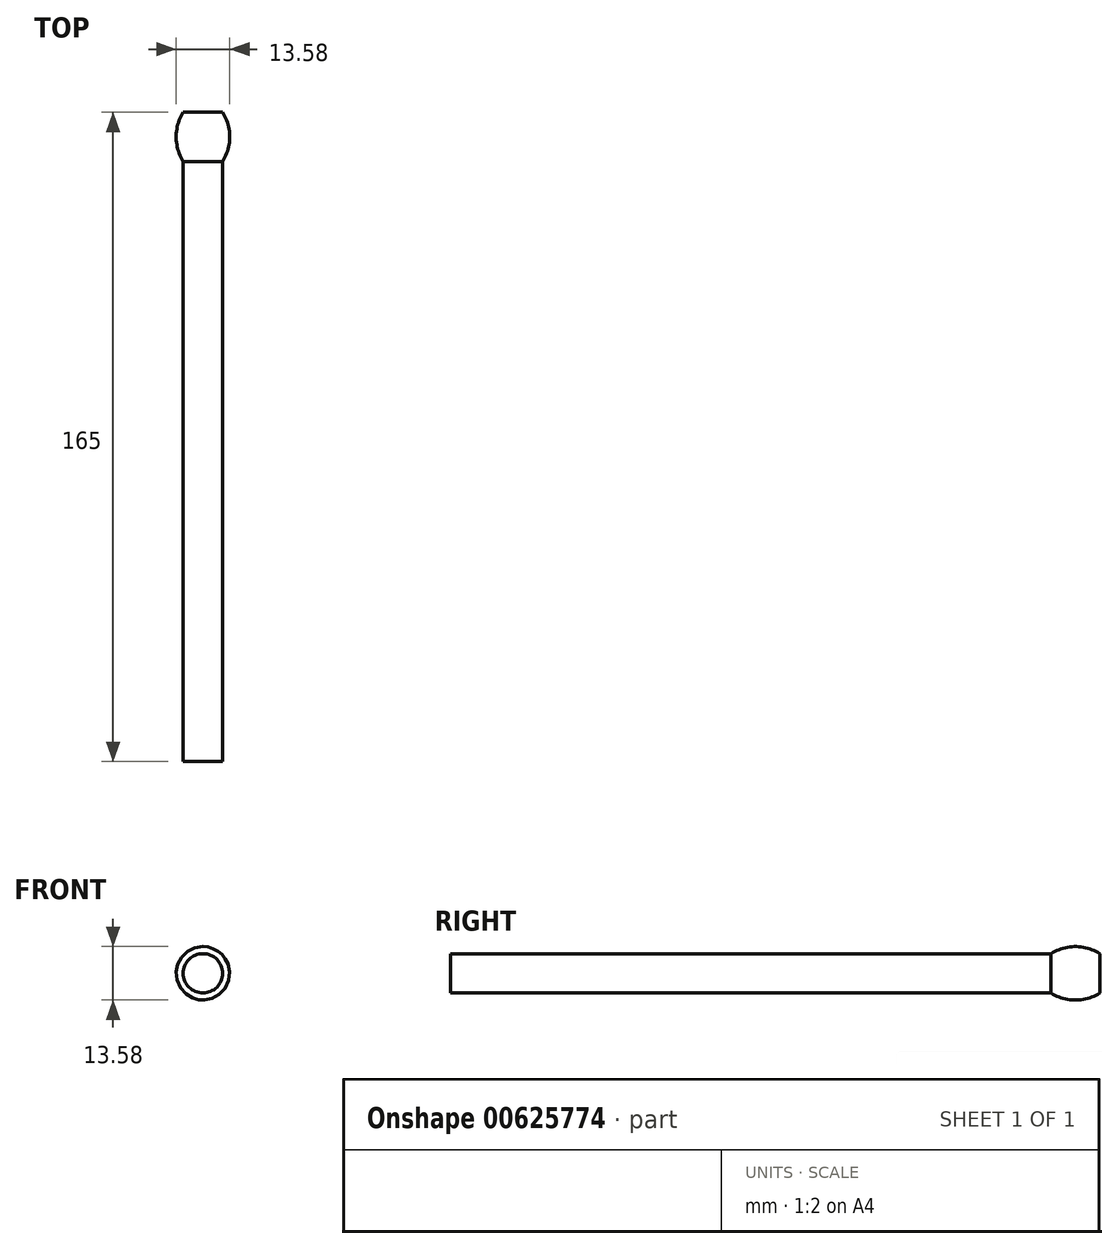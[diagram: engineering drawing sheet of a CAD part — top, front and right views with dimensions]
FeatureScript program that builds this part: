
annotation { "Feature Type Name" : "Feature", "Feature Type Description" : "" }
export const myFeature = defineFeature(function(context is Context, id is Id, definition is map)
    precondition{}
    {
        {
            var Q0;
            Q0=qCreatedBy(makeId("Top.planeOp"),FACE);
            var sketch = newSketch(context, id + "F0", { "sketchPlane" : qUnion([Q0])});
            skLineSegment(sketch, "E0", {"start": v(0, 82.5) * mm, "end": v(5, 82.5) * mm});
            skLineSegment(sketch, "E1", {"start": v(5, 82.5) * mm, "end": v(5, 0) * mm});
            skLineSegment(sketch, "E2", {"start": v(-8.16, 76.25) * mm, "end": v(26.14, 76.25) * mm, "construction": true});
            skPoint(sketch, "E3", {"position": v(-5, 76.25) * mm});
            skArc(sketch, "E4", {"start": v(5, 70) * mm, "mid": v(6.8, 76.25) * mm, "end": v(5, 82.5) * mm});
            skLineSegment(sketch, "E5", {"start": v(-18.01, 0) * mm, "end": v(22.76, 0) * mm, "construction": true});
            skLineSegment(sketch, "E6.MirrorCS", {"start": v(5, -82.5) * mm, "end": v(5, 0) * mm});
            skArc(sketch, "E7.MirrorCS", {"start": v(5, -70) * mm, "mid": v(6.8, -76.25) * mm, "end": v(5, -82.5) * mm});
            skLineSegment(sketch, "E8.MirrorCS", {"start": v(-8.16, -76.25) * mm, "end": v(26.14, -76.25) * mm, "construction": true});
            skLineSegment(sketch, "E9.MirrorCS", {"start": v(0, -82.5) * mm, "end": v(5, -82.5) * mm});
            skLineSegment(sketch, "E10", {"start": v(0, 82.5) * mm, "end": v(0, -82.5) * mm});
            skSolve(sketch);
        }
        {
            var Q0;
            {var subQ8=sQuery(id+"F0.wireOp",EDGE,"E0");Q0=makeQuery(id+"F0.imprint","IMPRINT",FACE,{"disambiguationData":[TD([[makeQuery(id+"F0.imprint","IMPRINT",EDGE,{"derivedFrom":subQ8}),-1.0]])]});}
            var Q1;
            {var subQ0=sQuery(id+"F0.wireOp",EDGE,"E4");Q1=makeQuery(id+"F0.imprint","IMPRINT",FACE,{"disambiguationData":[TD([[makeQuery(id+"F0.imprint","IMPRINT",EDGE,{"derivedFrom":subQ0}),1.0]])]});}
            var Q2;
            {var subQ0=sQuery(id+"F0.wireOp",EDGE,"E7.MirrorCS");Q2=makeQuery(id+"F0.imprint","IMPRINT",FACE,{"disambiguationData":[TD([[makeQuery(id+"F0.imprint","IMPRINT",EDGE,{"derivedFrom":subQ0}),-1.0]])]});}
            var Q3;
            Q3=sQuery(id+"F0.wireOp",EDGE,"E10");
            revolve(context, id + "F1", {"surfaceOperationType" : NewSurfaceOperationType.NEW, "entities" : qUnion([Q0, Q1, Q2]), "axis" : qUnion([Q3]), "revolveType" : RevolveType.FULL});
        }
    });
